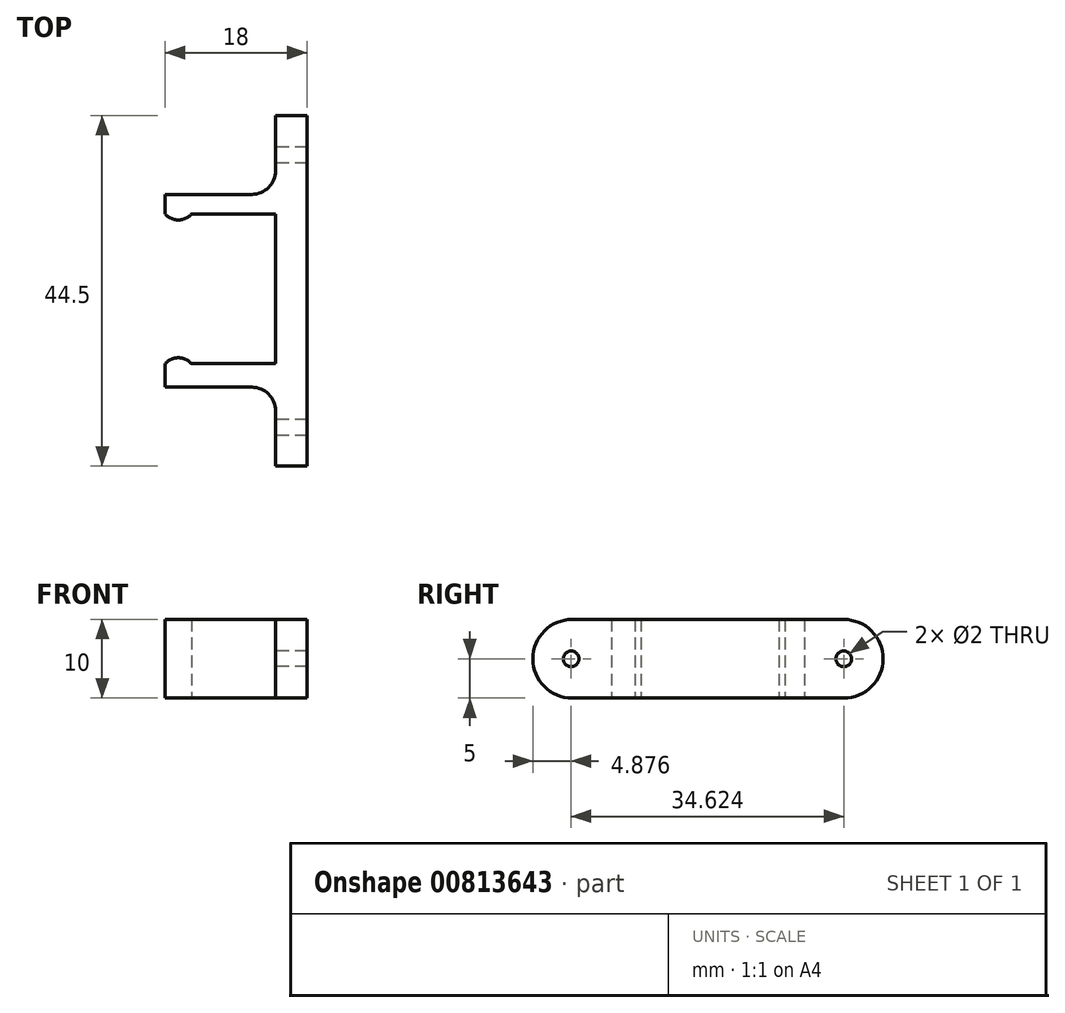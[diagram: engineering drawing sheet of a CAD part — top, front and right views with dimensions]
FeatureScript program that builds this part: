
annotation { "Feature Type Name" : "Feature", "Feature Type Description" : "" }
export const myFeature = defineFeature(function(context is Context, id is Id, definition is map)
    precondition{}
    {
        {
            var Q0;
            Q0=qCreatedBy(makeId("Top.planeOp"),FACE);
            var sketch = newSketch(context, id + "F0", { "sketchPlane" : qUnion([Q0])});
            skLineSegment(sketch, "E0.right", {"start": v(2, -12.25) * mm, "end": v(2, 12.25) * mm});
            skPoint(sketch, "E0.middle", {"position": v(0, 0) * mm});
            skLineSegment(sketch, "E1.bottom", {"start": v(-2, 12.25) * mm, "end": v(-16, 12.25) * mm});
            skLineSegment(sketch, "E1.top", {"start": v(-2, 9.75) * mm, "end": v(-16, 9.75) * mm});
            skLineSegment(sketch, "E1.right", {"start": v(-16, 12.25) * mm, "end": v(-16, 9.75) * mm});
            skLineSegment(sketch, "E2.bottom", {"start": v(-2, -12.25) * mm, "end": v(-16, -12.25) * mm});
            skLineSegment(sketch, "E2.top", {"start": v(-2, -9.25) * mm, "end": v(-16, -9.25) * mm});
            skLineSegment(sketch, "E2.right", {"start": v(-16, -12.25) * mm, "end": v(-16, -9.25) * mm});
            skArc(sketch, "E3", {"start": v(-16, 9.75) * mm, "mid": v(-14.35, 9) * mm, "end": v(-12.7, 9.75) * mm});
            skArc(sketch, "E4", {"start": v(-12.7, -9.25) * mm, "mid": v(-14.35, -8.5) * mm, "end": v(-16, -9.25) * mm});
            skLineSegment(sketch, "E5.top", {"start": v(2, 22.25) * mm, "end": v(-2, 22.25) * mm});
            skLineSegment(sketch, "E5.left", {"start": v(2, 12.25) * mm, "end": v(2, 22.25) * mm});
            skLineSegment(sketch, "E5.right", {"start": v(-2, 12.25) * mm, "end": v(-2, 22.25) * mm});
            skLineSegment(sketch, "E6.top", {"start": v(2, -22.25) * mm, "end": v(-2, -22.25) * mm});
            skLineSegment(sketch, "E6.left", {"start": v(2, -12.25) * mm, "end": v(2, -22.25) * mm});
            skLineSegment(sketch, "E6.right", {"start": v(-2, -12.25) * mm, "end": v(-2, -22.25) * mm});
            skLineSegment(sketch, "E7", {"start": v(-2, 9.75) * mm, "end": v(-2, -9.25) * mm});
            skSolve(sketch);
        }
        {
            var Q0;
            {var subQ0=sQuery(id+"F0.wireOp",EDGE,"E3");Q0=makeQuery(id+"F0.imprint","IMPRINT",FACE,{"disambiguationData":[TD([[makeQuery(id+"F0.imprint","IMPRINT",EDGE,{"derivedFrom":subQ0}),1.0]])]});}
            var Q1;
            Q1=makeQuery(id+"F0.imprint","IMPRINT",FACE,{"disambiguationData":[TD([[makeQuery(id+"F0.imprint","IMPRINT",EDGE,{"derivedFrom":sQuery(id+"F0.wireOp",EDGE,"E1.bottom")}),1.0]])]});
            var Q2;
            Q2=makeQuery(id+"F0.imprint","IMPRINT",FACE,{"disambiguationData":[TD([[makeQuery(id+"F0.imprint","IMPRINT",EDGE,{"derivedFrom":sQuery(id+"F0.wireOp",EDGE,"E0.bottom")}),1.0]])]});
            var Q3;
            {var subQ0=sQuery(id+"F0.wireOp",EDGE,"E4");Q3=makeQuery(id+"F0.imprint","IMPRINT",FACE,{"disambiguationData":[TD([[makeQuery(id+"F0.imprint","IMPRINT",EDGE,{"derivedFrom":subQ0}),1.0]])]});}
            var Q4;
            Q4=makeQuery(id+"F0.imprint","IMPRINT",FACE,{"disambiguationData":[TD([[makeQuery(id+"F0.imprint","IMPRINT",EDGE,{"derivedFrom":sQuery(id+"F0.wireOp",EDGE,"E2.bottom")}),-1.0]])]});
            extrude(context, id + "F1", {"entities" : qUnion([Q0, Q1, Q2, Q3, Q4]), "depth" : 10 * mm, "offsetDistance" : 25 * mm});
        }
        {
            var Q0;
            Q0=makeQuery(id+"F1.opExtrude","SWEPT_FACE",FACE,{"disambiguationData":[OSD([sQuery(id+"F0.wireOp",EDGE,"E5.right")])]});
            var sketch = newSketch(context, id + "F2", { "sketchPlane" : qUnion([Q0])});
            skLineSegment(sketch, "E8", {"start": v(-22.25, 10) * mm, "end": v(-12.25, 0) * mm, "construction": true});
            skLineSegment(sketch, "E9", {"start": v(-12.25, 0) * mm, "end": v(-22.25, 0) * mm, "construction": true});
            skLineSegment(sketch, "E10", {"start": v(-22.25, 0) * mm, "end": v(-12.25, 10) * mm, "construction": true});
            skLineSegment(sketch, "E11", {"start": v(21.8, 10) * mm, "end": v(12.94, 0) * mm, "construction": true});
            skLineSegment(sketch, "E12", {"start": v(12.94, 0) * mm, "end": v(12.94, 10) * mm, "construction": true});
            skLineSegment(sketch, "E13", {"start": v(12.94, 10) * mm, "end": v(21.8, 0) * mm, "construction": true});
            skPoint(sketch, "E14", {"position": v(-17.25, 5) * mm});
            skPoint(sketch, "E15", {"position": v(17.37, 5) * mm});
            skSolve(sketch);
        }
        {
            var Q0;
            Q0=sQuery(id+"F2.wireOp",VERTEX,"E14");
            var Q1;
            Q1=sQuery(id+"F2.wireOp",VERTEX,"E15");
            var Q2;
            Q2=makeQuery(id+"F1.opExtrude","SWEPT_BODY",BODY,{"disambiguationData":[OSD([sQuery(id+"F0.wireOp",EDGE,"E0.right"),sQuery(id+"F0.wireOp",EDGE,"E1.bottom"),sQuery(id+"F0.wireOp",EDGE,"E1.top"),sQuery(id+"F0.wireOp",EDGE,"E1.right"),sQuery(id+"F0.wireOp",EDGE,"E2.bottom"),sQuery(id+"F0.wireOp",EDGE,"E2.top"),sQuery(id+"F0.wireOp",EDGE,"E2.right"),sQuery(id+"F0.wireOp",EDGE,"E3"),sQuery(id+"F0.wireOp",EDGE,"E4"),sQuery(id+"F0.wireOp",EDGE,"E5.top"),sQuery(id+"F0.wireOp",EDGE,"E5.left"),sQuery(id+"F0.wireOp",EDGE,"E5.right"),sQuery(id+"F0.wireOp",EDGE,"E6.top"),sQuery(id+"F0.wireOp",EDGE,"E6.left"),sQuery(id+"F0.wireOp",EDGE,"E6.right"),sQuery(id+"F0.wireOp",EDGE,"E7")])]});
            hole(context, id + "F3", {"style" : HoleStyle.SIMPLE, "endStyle" : HoleEndStyle.THROUGH, "holeDiameter" : 2 * mm, "majorDiameter" : 5 * mm, "isTappedThrough" : true, "tappedDepth" : 12 * mm, "tapClearance" : 3, "locations" : qUnion([Q0, Q1]), "scope" : qUnion([Q2])});
        }
        {
            var Q0;
            Q0=makeQuery(id+"F1.opExtrude","CAP_EDGE",EDGE,{"disambiguationData":[OSD([sQuery(id+"F0.wireOp",EDGE,"E5.top")])],"isStart":false});
            var Q1;
            Q1=makeQuery(id+"F1.opExtrude","CAP_EDGE",EDGE,{"disambiguationData":[OSD([sQuery(id+"F0.wireOp",EDGE,"E6.top")])],"isStart":false});
            var Q2;
            Q2=makeQuery(id+"F1.opExtrude","CAP_EDGE",EDGE,{"disambiguationData":[OSD([sQuery(id+"F0.wireOp",EDGE,"E6.top")])],"isStart":true});
            var Q3;
            Q3=makeQuery(id+"F1.opExtrude","CAP_EDGE",EDGE,{"disambiguationData":[OSD([sQuery(id+"F0.wireOp",EDGE,"E5.top")])],"isStart":true});
            fillet(context, id + "F4", {"entities" : qUnion([Q0, Q1, Q2, Q3]), "radius" : 5 * mm, "tangentPropagation" : true, "allowEdgeOverflow" : false});
        }
        {
            var Q0;
            Q0=makeQuery(id+"F1.opExtrude","SWEPT_EDGE",EDGE,{"disambiguationData":[OSD([sQuery(id+"F0.wireOp",EDGE,"E1.bottom"),sQuery(id+"F0.wireOp",EDGE,"E5.right")])]});
            var Q1;
            Q1=makeQuery(id+"F1.opExtrude","SWEPT_EDGE",EDGE,{"disambiguationData":[OSD([sQuery(id+"F0.wireOp",EDGE,"E2.bottom"),sQuery(id+"F0.wireOp",EDGE,"E6.right")])]});
            fillet(context, id + "F5", {"entities" : qUnion([Q0, Q1]), "radius" : 3 * mm, "tangentPropagation" : true, "allowEdgeOverflow" : false});
        }
    });
